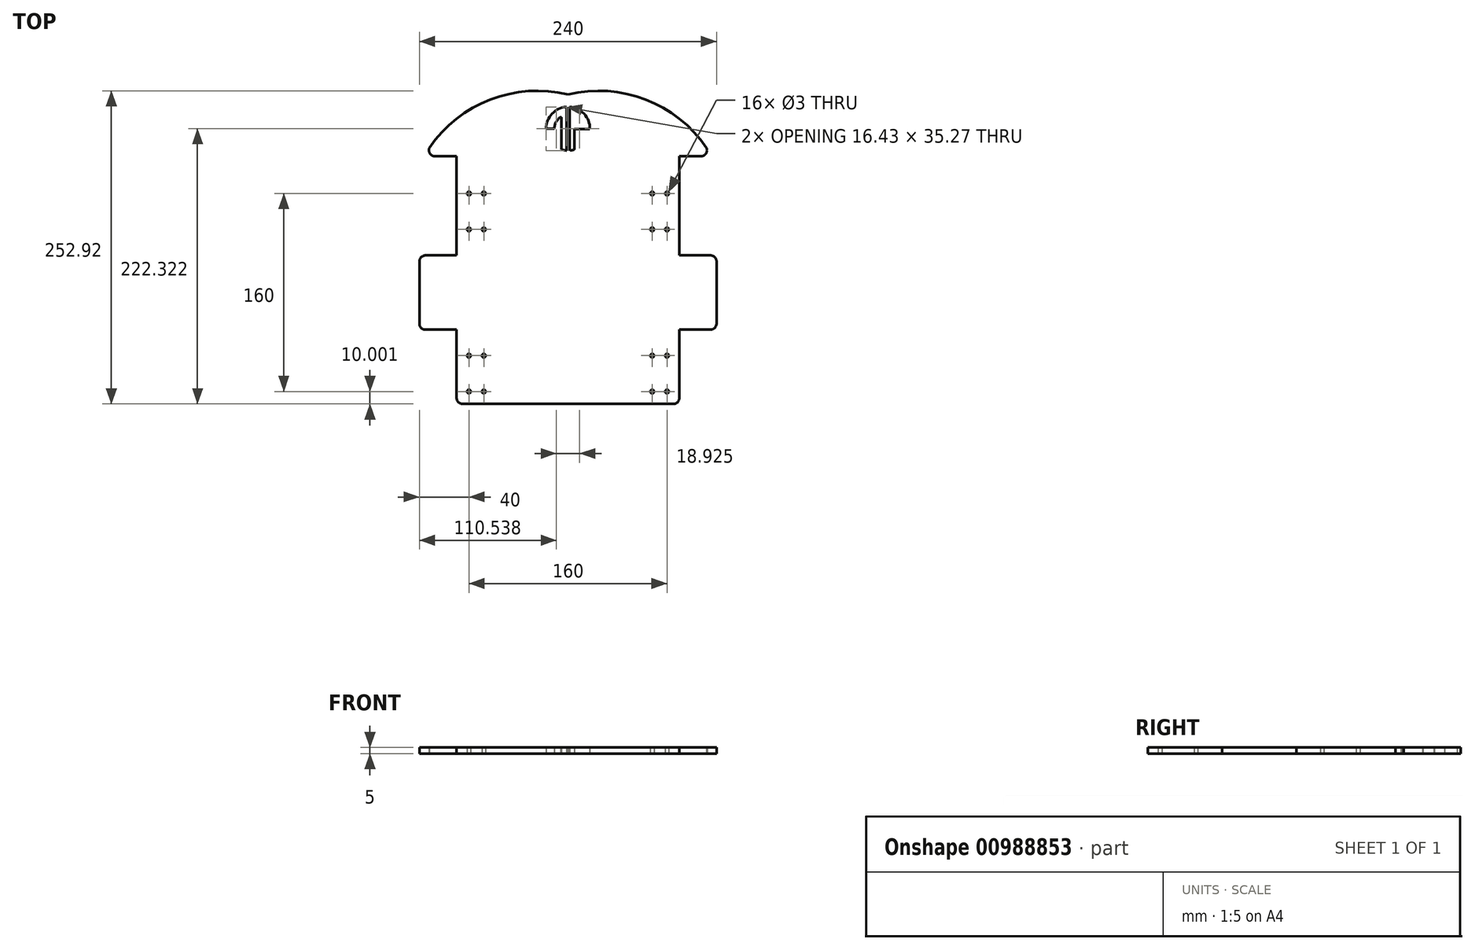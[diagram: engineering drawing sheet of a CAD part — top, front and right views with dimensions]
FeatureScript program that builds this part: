
annotation { "Feature Type Name" : "Feature", "Feature Type Description" : "" }
export const myFeature = defineFeature(function(context is Context, id is Id, definition is map)
    precondition{}
    {
        {
            var Q0;
            Q0=qCreatedBy(makeId("Top.planeOp"),FACE);
            var sketch = newSketch(context, id + "F0", { "sketchPlane" : qUnion([Q0])});
            skLineSegment(sketch, "E0", {"start": v(0, -139.79) * mm, "end": v(-85, -139.79) * mm});
            skLineSegment(sketch, "E1", {"start": v(-90, -134.79) * mm, "end": v(-90, -79.79) * mm});
            skLineSegment(sketch, "E2", {"start": v(-90, -79.79) * mm, "end": v(-115, -79.79) * mm});
            skLineSegment(sketch, "E3", {"start": v(-120, -74.79) * mm, "end": v(-120, -24.79) * mm});
            skLineSegment(sketch, "E4", {"start": v(-115, -19.79) * mm, "end": v(-90, -19.79) * mm});
            skLineSegment(sketch, "E5", {"start": v(-90, -19.79) * mm, "end": v(-90, 60.21) * mm});
            skLineSegment(sketch, "E6", {"start": v(-90, 60.21) * mm, "end": v(-107.33, 60.21) * mm});
            skLineSegment(sketch, "E7.MirrorCS", {"start": v(90, 60.21) * mm, "end": v(107.33, 60.21) * mm});
            skLineSegment(sketch, "E8.MirrorCS", {"start": v(90, -19.79) * mm, "end": v(90, 60.21) * mm});
            skLineSegment(sketch, "E9.MirrorCS", {"start": v(115, -19.79) * mm, "end": v(90, -19.79) * mm});
            skLineSegment(sketch, "E10.MirrorCS", {"start": v(120, -74.79) * mm, "end": v(120, -24.79) * mm});
            skLineSegment(sketch, "E11.MirrorCS", {"start": v(90, -79.79) * mm, "end": v(115, -79.79) * mm});
            skLineSegment(sketch, "E12.MirrorCS", {"start": v(90, -134.79) * mm, "end": v(90, -79.79) * mm});
            skLineSegment(sketch, "E13.MirrorCS", {"start": v(0, -139.79) * mm, "end": v(85, -139.79) * mm});
            skPoint(sketch, "E14.visualSharp", {"position": v(120, -19.79) * mm});
            skArc(sketch, "E14.filletArc", {"start": v(120, -24.79) * mm, "mid": v(118.54, -21.25) * mm, "end": v(115, -19.79) * mm});
            skPoint(sketch, "E15.visualSharp", {"position": v(120, -79.79) * mm});
            skArc(sketch, "E15.filletArc", {"start": v(115, -79.79) * mm, "mid": v(118.54, -78.32) * mm, "end": v(120, -74.79) * mm});
            skPoint(sketch, "E16.visualSharp", {"position": v(90, -139.79) * mm});
            skArc(sketch, "E16.filletArc", {"start": v(85, -139.79) * mm, "mid": v(88.54, -138.32) * mm, "end": v(90, -134.79) * mm});
            skPoint(sketch, "E17.visualSharp", {"position": v(-90, -139.79) * mm});
            skArc(sketch, "E17.filletArc", {"start": v(-90, -134.79) * mm, "mid": v(-88.54, -138.32) * mm, "end": v(-85, -139.79) * mm});
            skPoint(sketch, "E18.visualSharp", {"position": v(-120, -79.79) * mm});
            skArc(sketch, "E18.filletArc", {"start": v(-120, -74.79) * mm, "mid": v(-118.54, -78.32) * mm, "end": v(-115, -79.79) * mm});
            skPoint(sketch, "E19.visualSharp", {"position": v(-120, -19.79) * mm});
            skArc(sketch, "E19.filletArc", {"start": v(-115, -19.79) * mm, "mid": v(-118.54, -21.25) * mm, "end": v(-120, -24.79) * mm});
            skPoint(sketch, "E20.visualSharp", {"position": v(-120, 60.21) * mm});
            skArc(sketch, "E20.filletArc", {"start": v(-110.6, 69) * mm, "mid": v(-112.02, 63.47) * mm, "end": v(-107.33, 60.21) * mm});
            skPoint(sketch, "E21.visualSharp", {"position": v(120, 60.21) * mm});
            skArc(sketch, "E21.filletArc", {"start": v(107.33, 60.21) * mm, "mid": v(112.02, 63.47) * mm, "end": v(110.6, 69) * mm});
            skCircle(sketch, "E22", {"center": v(-80, -129.79) * mm, "radius": 1.5 * mm});
            skCircle(sketch, "E23", {"center": v(-68, -129.79) * mm, "radius": 1.5 * mm});
            skCircle(sketch, "E24", {"center": v(-80, -100.79) * mm, "radius": 1.5 * mm});
            skCircle(sketch, "E25", {"center": v(-68, -100.79) * mm, "radius": 1.5 * mm});
            skCircle(sketch, "E26.MirrorC", {"center": v(80, -100.79) * mm, "radius": 1.5 * mm});
            skCircle(sketch, "E27.MirrorC", {"center": v(68, -100.79) * mm, "radius": 1.5 * mm});
            skCircle(sketch, "E28.MirrorC", {"center": v(80, -129.79) * mm, "radius": 1.5 * mm});
            skCircle(sketch, "E29.MirrorC", {"center": v(68, -129.79) * mm, "radius": 1.5 * mm});
            skCircle(sketch, "E30.MirrorC", {"center": v(-80, 1.21) * mm, "radius": 1.5 * mm});
            skCircle(sketch, "E31.MirrorC", {"center": v(-68, 1.21) * mm, "radius": 1.5 * mm});
            skCircle(sketch, "E32.MirrorC", {"center": v(-80, 30.21) * mm, "radius": 1.5 * mm});
            skCircle(sketch, "E33.MirrorC", {"center": v(-68, 30.21) * mm, "radius": 1.5 * mm});
            skCircle(sketch, "E34.MirrorC", {"center": v(68, 30.21) * mm, "radius": 1.5 * mm});
            skCircle(sketch, "E35.MirrorC", {"center": v(80, 30.21) * mm, "radius": 1.5 * mm});
            skCircle(sketch, "E36.MirrorC", {"center": v(80, 1.21) * mm, "radius": 1.5 * mm});
            skCircle(sketch, "E37.MirrorC", {"center": v(68, 1.21) * mm, "radius": 1.5 * mm});
            skPoint(sketch, "E38.orphan", {"position": v(-120, -49.79) * mm});
            skPoint(sketch, "E39.end.orphan", {"position": v(120, -49.79) * mm});
            skPoint(sketch, "E40.orphan", {"position": v(0, 110.21) * mm});
            skLineSegment(sketch, "E41", {"start": v(5.25, 82.22) * mm, "end": v(5.25, 65.65) * mm});
            skArc(sketch, "E42", {"start": v(-1.25, 100.17) * mm, "mid": v(-12.93, 94.58) * mm, "end": v(-17.68, 82.54) * mm});
            skArc(sketch, "E43", {"start": v(-5.25, 92.2) * mm, "mid": v(-9.45, 88.16) * mm, "end": v(-11, 82.54) * mm});
            skLineSegment(sketch, "E44", {"start": v(-17.68, 82.54) * mm, "end": v(-11, 82.54) * mm});
            skPoint(sketch, "E45.startSnap0", {"position": v(5.25, 82.22) * mm});
            skLineSegment(sketch, "E46", {"start": v(-1.25, 65.03) * mm, "end": v(-1.25, 82.54) * mm});
            skLineSegment(sketch, "E47", {"start": v(1.25, 65.03) * mm, "end": v(1.25, 82.53) * mm});
            skLineSegment(sketch, "E48", {"start": v(-1.25, 65.03) * mm, "end": v(-1.25, 100.17) * mm});
            skLineSegment(sketch, "E49", {"start": v(1.25, 65.03) * mm, "end": v(1.25, 100.17) * mm});
            skArc(sketch, "E50.trimOffspring", {"start": v(17.68, 82.22) * mm, "mid": v(13.04, 94.47) * mm, "end": v(1.25, 100.17) * mm});
            skLineSegment(sketch, "E51", {"start": v(-1.25, 100.17) * mm, "end": v(-1.25, 82.54) * mm});
            skLineSegment(sketch, "E52", {"start": v(1.25, 100.17) * mm, "end": v(1.25, 64.9) * mm});
            skPoint(sketch, "E53.start.orphan", {"position": v(0, 65.03) * mm});
            skArc(sketch, "E54.trimOffspring", {"start": v(1.25, 64.9) * mm, "mid": v(3.27, 65.16) * mm, "end": v(5.25, 65.65) * mm});
            skLineSegment(sketch, "E55", {"start": v(17.68, 82.22) * mm, "end": v(5.25, 82.22) * mm});
            skPoint(sketch, "E56.endSnap0", {"position": v(-2.76, 65.07) * mm});
            skLineSegment(sketch, "E57", {"start": v(-5.25, 65.65) * mm, "end": v(-5.25, 92.2) * mm});
            skArc(sketch, "E58", {"start": v(-5.25, 65.65) * mm, "mid": v(-3.27, 65.16) * mm, "end": v(-1.25, 64.9) * mm});
            skLineSegment(sketch, "E59.trimOffspring", {"start": v(-1.25, 65.03) * mm, "end": v(-1.25, 64.9) * mm});
            skLineSegment(sketch, "E60", {"start": v(-112.02, 66.96) * mm, "end": v(-112.02, 65.03) * mm});
            skPoint(sketch, "E60.startSnap0", {"position": v(-112.02, 63.47) * mm});
            skLineSegment(sketch, "E61", {"start": v(-49.36, 110.21) * mm, "end": v(49.36, 110.21) * mm});
            skPoint(sketch, "E61.endSnap0", {"position": v(112.02, 63.47) * mm});
            skLineSegment(sketch, "E62", {"start": v(112.02, 66.96) * mm, "end": v(112.02, 63.47) * mm});
            skPoint(sketch, "E63.visualSharp", {"position": v(-112.02, 110.21) * mm});
            skPoint(sketch, "E64.orphan", {"position": v(112.02, 110.21) * mm});
            skPoint(sketch, "E65.visualSharp", {"position": v(77.02, 110.21) * mm});
            skLineSegment(sketch, "E65.filletArc", {"start": v(77.02, 110.21) * mm, "end": v(77.02, 110.21) * mm});
            skArc(sketch, "E66", {"start": v(-5.25, 91.24) * mm, "mid": v(-5.54, 91.78) * mm, "end": v(-6.14, 91.66) * mm});
            skPoint(sketch, "E66.first.point", {"position": v(-6.14, 91.66) * mm});
            skPoint(sketch, "E66.second.point", {"position": v(-5.25, 91.39) * mm});
            skArc(sketch, "E67", {"start": v(0, 110.21) * mm, "mid": v(-62.75, 106.04) * mm, "end": v(-112.02, 66.96) * mm});
            skArc(sketch, "E68.MirrorCS", {"start": v(0, 110.21) * mm, "mid": v(62.75, 106.04) * mm, "end": v(112.02, 66.96) * mm});
            skPoint(sketch, "E63.filletArc.start.orphan", {"position": v(-77.02, 110.21) * mm});
            skPoint(sketch, "E69.orphan", {"position": v(-112.02, 75.21) * mm});
            skPoint(sketch, "E70.orphan", {"position": v(112.02, 75.21) * mm});
            skSolve(sketch);
        }
        {
            var Q0;
            Q0 = qSketchRegion(id + "F0", true);
            extrude(context, id + "F1", {"entities" : qUnion([Q0]), "depth" : 5 * mm, "offsetDistance" : 25 * mm});
        }
    });
